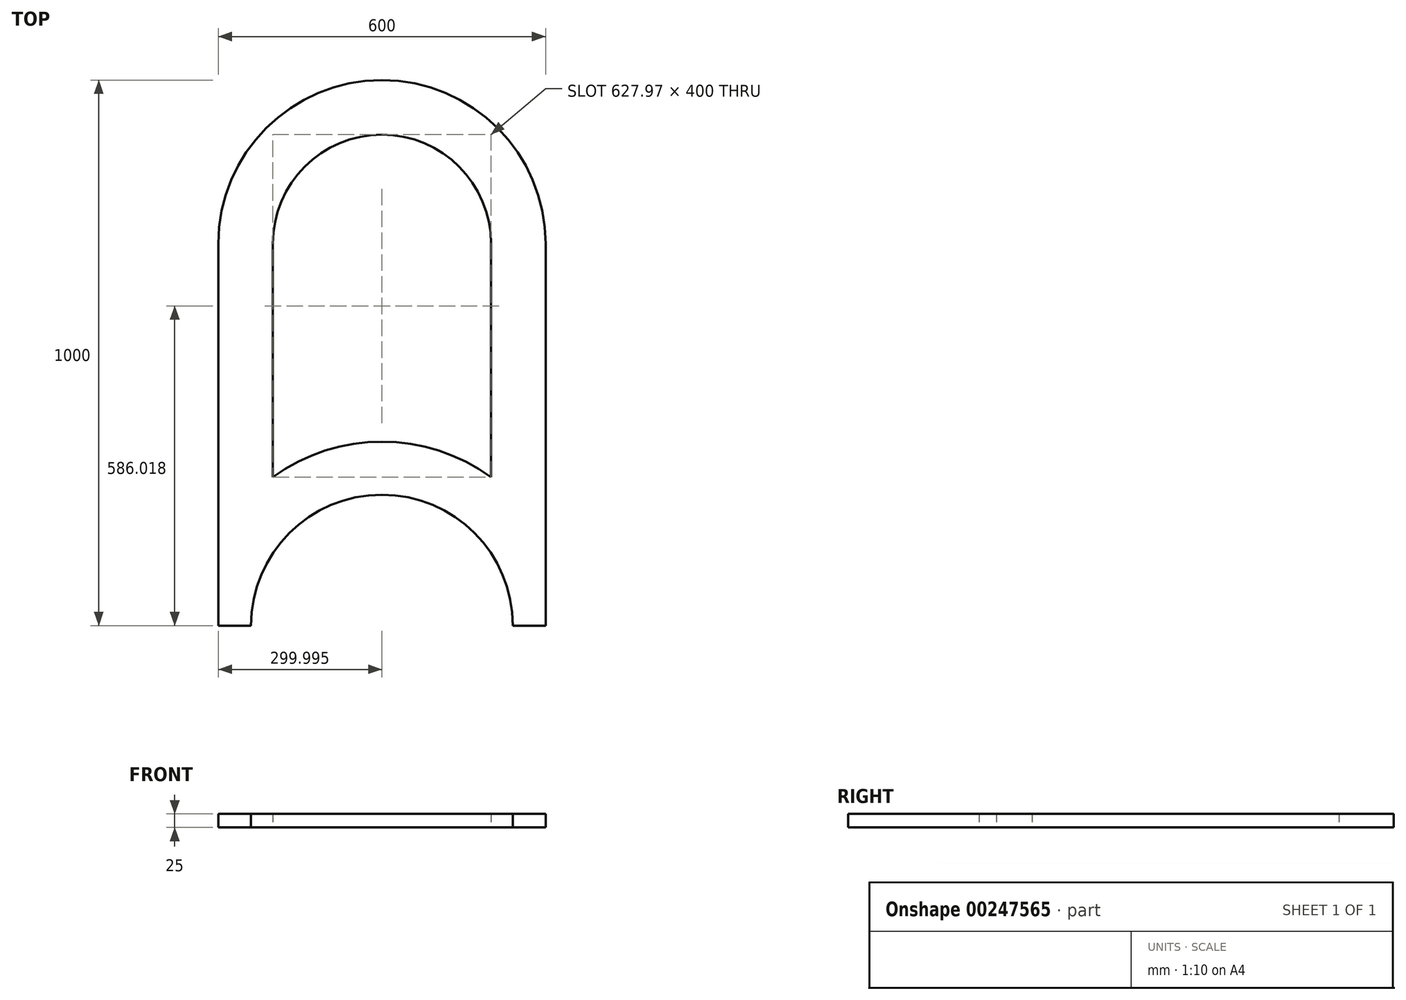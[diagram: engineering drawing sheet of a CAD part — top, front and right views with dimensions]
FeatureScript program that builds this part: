
annotation { "Feature Type Name" : "Feature", "Feature Type Description" : "" }
export const myFeature = defineFeature(function(context is Context, id is Id, definition is map)
    precondition{}
    {
        {
            var Q0;
            Q0=qCreatedBy(makeId("Top.planeOp"),FACE);
            var sketch = newSketch(context, id + "F0", { "sketchPlane" : qUnion([Q0])});
            skLineSegment(sketch, "E0", {"start": v(-255.48, -48.27) * mm, "end": v(-195.48, -48.27) * mm});
            skLineSegment(sketch, "E1", {"start": v(284.52, -48.27) * mm, "end": v(344.52, -48.27) * mm});
            skArc(sketch, "E2", {"start": v(284.52, -48.27) * mm, "mid": v(44.52, 191.73) * mm, "end": v(-195.48, -48.27) * mm});
            skLineSegment(sketch, "E3", {"start": v(344.52, -48.27) * mm, "end": v(344.52, 651.73) * mm});
            skPoint(sketch, "E4", {"position": v(44.52, 851.73) * mm});
            skPoint(sketch, "E5", {"position": v(44.52, 951.73) * mm});
            skPoint(sketch, "E6", {"position": v(-255.48, 851.73) * mm});
            skPoint(sketch, "E7", {"position": v(-255.48, 951.73) * mm});
            skPoint(sketch, "E8", {"position": v(-255.48, 751.73) * mm});
            skPoint(sketch, "E9", {"position": v(44.52, 751.73) * mm});
            skLineSegment(sketch, "E10", {"start": v(44.52, 851.92) * mm, "end": v(44.52, 851.73) * mm});
            skLineSegment(sketch, "E11", {"start": v(-255.48, -48.27) * mm, "end": v(-255.48, 651.73) * mm});
            skPoint(sketch, "E12", {"position": v(-155.48, 751.73) * mm});
            skPoint(sketch, "E13", {"position": v(244.52, 751.73) * mm});
            skPoint(sketch, "E14", {"position": v(44.52, 191.73) * mm});
            skLineSegment(sketch, "E15", {"start": v(-155.48, 651.73) * mm, "end": v(-155.48, 223.76) * mm});
            skLineSegment(sketch, "E16", {"start": v(244.52, 651.73) * mm, "end": v(244.52, 223.76) * mm});
            skPoint(sketch, "E17.orphan", {"position": v(244.52, -48.27) * mm});
            skPoint(sketch, "E18", {"position": v(-155.48, 84.4) * mm});
            skPoint(sketch, "E19", {"position": v(244.52, 84.4) * mm});
            skPoint(sketch, "E20", {"position": v(-155.48, 184.4) * mm});
            skPoint(sketch, "E21", {"position": v(244.52, 184.4) * mm});
            skArc(sketch, "E22.trimOffspring", {"start": v(244.52, 223.76) * mm, "mid": v(44.52, 288.8) * mm, "end": v(-155.48, 223.76) * mm});
            skPoint(sketch, "E23", {"position": v(-255.48, 291.73) * mm});
            skLineSegment(sketch, "E24", {"start": v(344.52, 651.73) * mm, "end": v(344.52, 441.46) * mm});
            skLineSegment(sketch, "E25", {"start": v(344.52, 441.46) * mm, "end": v(344.52, 651.73) * mm});
            skPoint(sketch, "E26", {"position": v(44.52, 651.73) * mm});
            skArc(sketch, "E27", {"start": v(344.52, 651.73) * mm, "mid": v(44.52, 951.73) * mm, "end": v(-255.48, 651.73) * mm});
            skArc(sketch, "E28", {"start": v(244.52, 651.73) * mm, "mid": v(44.52, 851.73) * mm, "end": v(-155.48, 651.73) * mm});
            skPoint(sketch, "E29.orphan", {"position": v(-155.48, 951.73) * mm});
            skPoint(sketch, "E30.orphan", {"position": v(344.52, 951.73) * mm});
            skPoint(sketch, "E31.orphan", {"position": v(244.52, 951.73) * mm});
            skPoint(sketch, "E32.orphan", {"position": v(344.52, 851.73) * mm});
            skPoint(sketch, "E33.orphan", {"position": v(344.52, 751.73) * mm});
            skPoint(sketch, "E34.end.orphan", {"position": v(-274.95, 291.73) * mm});
            skPoint(sketch, "E35.end.orphan", {"position": v(44.52, 291.73) * mm});
            skSolve(sketch);
        }
        {
            var Q0;
            Q0=makeQuery(id+"F0.imprint","IMPRINT",FACE,{"disambiguationData":[TD([[makeQuery(id+"F0.imprint","IMPRINT",EDGE,{"derivedFrom":sQuery(id+"F0.wireOp",EDGE,"E0")}),1.0]])]});
            extrude(context, id + "F1", {"entities" : qUnion([Q0]), "depth" : 25 * mm});
        }
    });
